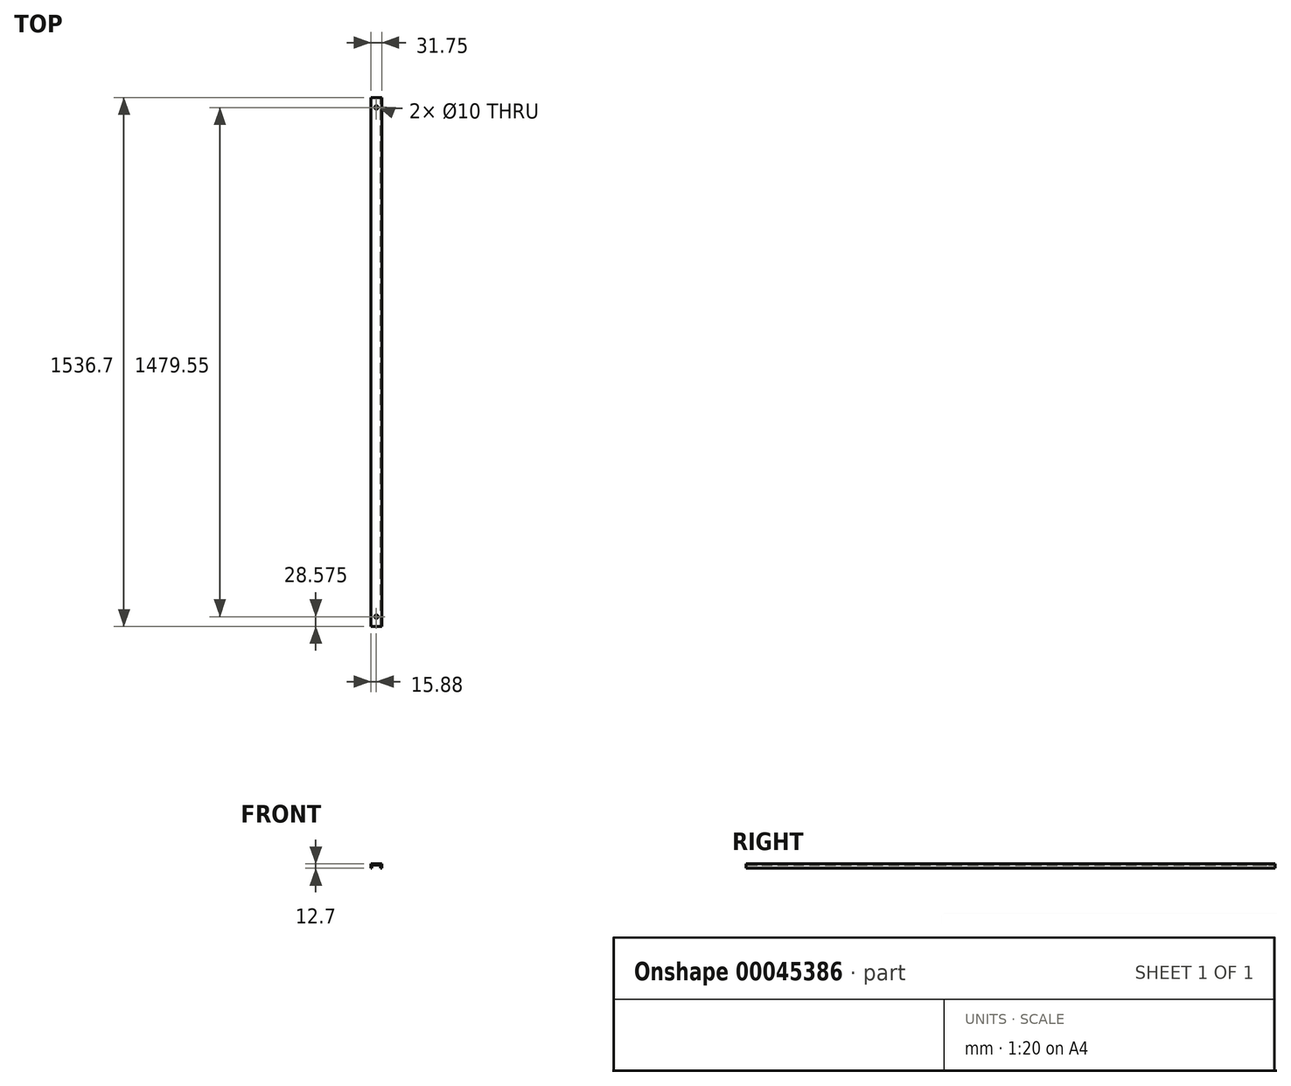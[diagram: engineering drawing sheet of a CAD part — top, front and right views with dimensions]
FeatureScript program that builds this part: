
annotation { "Feature Type Name" : "Feature", "Feature Type Description" : "" }
export const myFeature = defineFeature(function(context is Context, id is Id, definition is map)
    precondition{}
    {
        {
            var Q0;
            Q0=qCreatedBy(makeId("Front.planeOp"),FACE);
            var sketch = newSketch(context, id + "F0", { "sketchPlane" : qUnion([Q0])});
            skLineSegment(sketch, "E0.bottom", {"start": v(-14.14, -2.7) * mm, "end": v(17.61, -2.7) * mm});
            skLineSegment(sketch, "E0.top", {"start": v(-14.14, -15.4) * mm, "end": v(-10.96, -15.4) * mm});
            skLineSegment(sketch, "E0.left", {"start": v(-14.14, -2.7) * mm, "end": v(-14.14, -15.4) * mm});
            skLineSegment(sketch, "E0.right", {"start": v(17.61, -2.7) * mm, "end": v(17.61, -15.4) * mm});
            skLineSegment(sketch, "E1.top", {"start": v(-10.96, -5.87) * mm, "end": v(14.44, -5.87) * mm});
            skLineSegment(sketch, "E1.left", {"start": v(-10.96, -15.4) * mm, "end": v(-10.96, -5.87) * mm});
            skLineSegment(sketch, "E1.right", {"start": v(14.44, -15.4) * mm, "end": v(14.44, -5.87) * mm});
            skLineSegment(sketch, "E2.trimOffspring", {"start": v(14.44, -15.4) * mm, "end": v(17.61, -15.4) * mm});
            skSolve(sketch);
        }
        {
            var Q0;
            Q0 = qSketchRegion(id + "F0", true);
            extrude(context, id + "F1", {"entities" : qUnion([Q0]), "depth" : 1536.7 * mm});
        }
        {
            var Q0;
            Q0=makeQuery(id+"F1.opExtrude","SWEPT_FACE",FACE,{"disambiguationData":[OSD([sQuery(id+"F0.wireOp",EDGE,"E0.bottom")])]});
            var sketch = newSketch(context, id + "F2", { "sketchPlane" : qUnion([Q0])});
            skCircle(sketch, "E3", {"center": v(1.74, -28.58) * mm, "radius": 5 * mm});
            skCircle(sketch, "E4", {"center": v(1.74, -1508.13) * mm, "radius": 5 * mm});
            skSolve(sketch);
        }
        {
            var Q0;
            Q0=makeQuery(id+"F2.imprint","IMPRINT",FACE,{"disambiguationData":[TD([[makeQuery(id+"F2.imprint","IMPRINT",EDGE,{"derivedFrom":sQuery(id+"F2.wireOp",EDGE,"E4")}),1.0]])]});
            var Q1;
            Q1=makeQuery(id+"F2.imprint","IMPRINT",FACE,{"disambiguationData":[TD([[makeQuery(id+"F2.imprint","IMPRINT",EDGE,{"derivedFrom":sQuery(id+"F2.wireOp",EDGE,"E3")}),1.0]])]});
            extrude(context, id + "F3", {"entities" : qUnion([Q0, Q1]), "operationType" : NewBodyOperationType.REMOVE, "oppositeDirection" : true, "depth" : 25.4 * mm});
        }
    });
